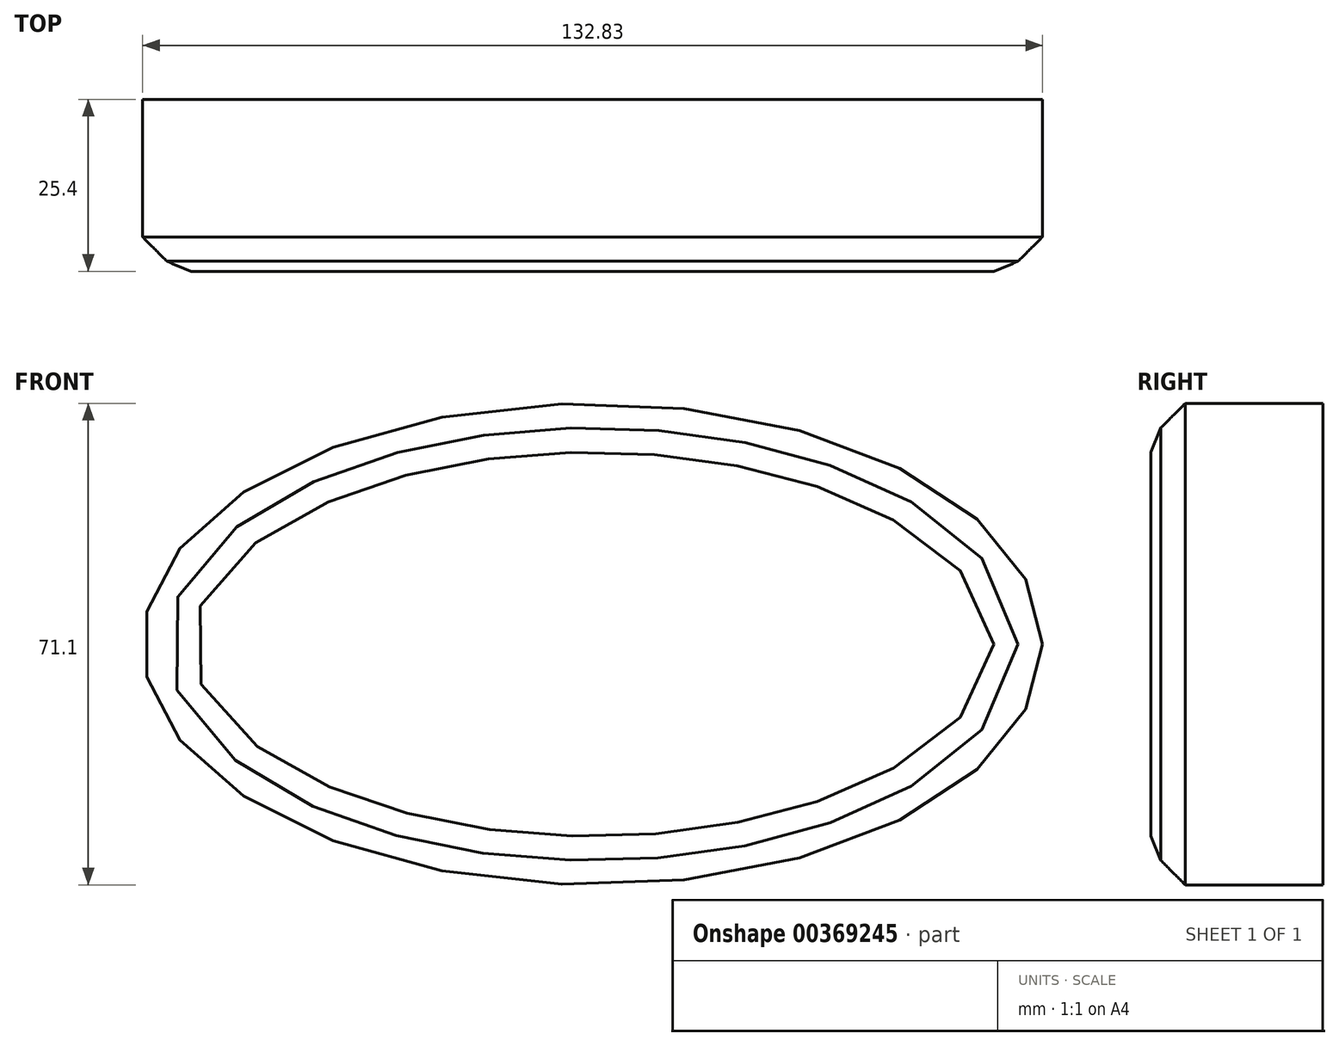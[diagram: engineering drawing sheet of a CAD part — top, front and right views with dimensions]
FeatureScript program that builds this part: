
annotation { "Feature Type Name" : "Feature", "Feature Type Description" : "" }
export const myFeature = defineFeature(function(context is Context, id is Id, definition is map)
    precondition{}
    {
        {
            var Q0;
            Q0=qCreatedBy(makeId("Front.planeOp"),FACE);
            var sketch = newSketch(context, id + "F0", { "sketchPlane" : qUnion([Q0])});
            skEllipse(sketch, "E0", {"center": v(-29.95, 23.42) * mm, "majorRadius": 66.41 * mm, "minorRadius": 35.55 * mm, "majorAxis": v(1, 0)});
            skSolve(sketch);
        }
        {
            var Q0;
            Q0 = qSketchRegion(id + "F0", true);
            extrude(context, id + "F1", {"entities" : qUnion([Q0]), "depth" : 25.4 * mm});
        }
        {
            var Q0;
            Q0=makeQuery(id+"F1.opExtrude","CAP_EDGE",EDGE,{"disambiguationData":[OSD([sQuery(id+"F0.wireOp",EDGE,"E0")])],"isStart":false});
            chamfer(context, id + "F2", {"entities" : qUnion([Q0]), "width" : 5.08 * mm, "tangentPropagation" : true});
        }
        {
            var Q0;
            {var subQ0=sQuery(id+"F0.wireOp",EDGE,"E0");Q0=makeQuery(id+"F2.opChamfer","BLEND_EDGE",EDGE,{"blendedFrom":[makeQuery(id+"F1.opExtrude","CAP_EDGE",EDGE,{"disambiguationData":[OSD([subQ0])],"isStart":false}),makeQuery(id+"F1.opExtrude","CAP_FACE",FACE,{"disambiguationData":[OSD([subQ0])],"isStart":false})],"blendedInto":[makeQuery(id+"F1.opExtrude","CAP_FACE",FACE,{"disambiguationData":[OSD([subQ0])],"isStart":false})]});}
            chamfer(context, id + "F3", {"entities" : qUnion([Q0]), "width" : 5.08 * mm, "tangentPropagation" : true});
        }
    });
